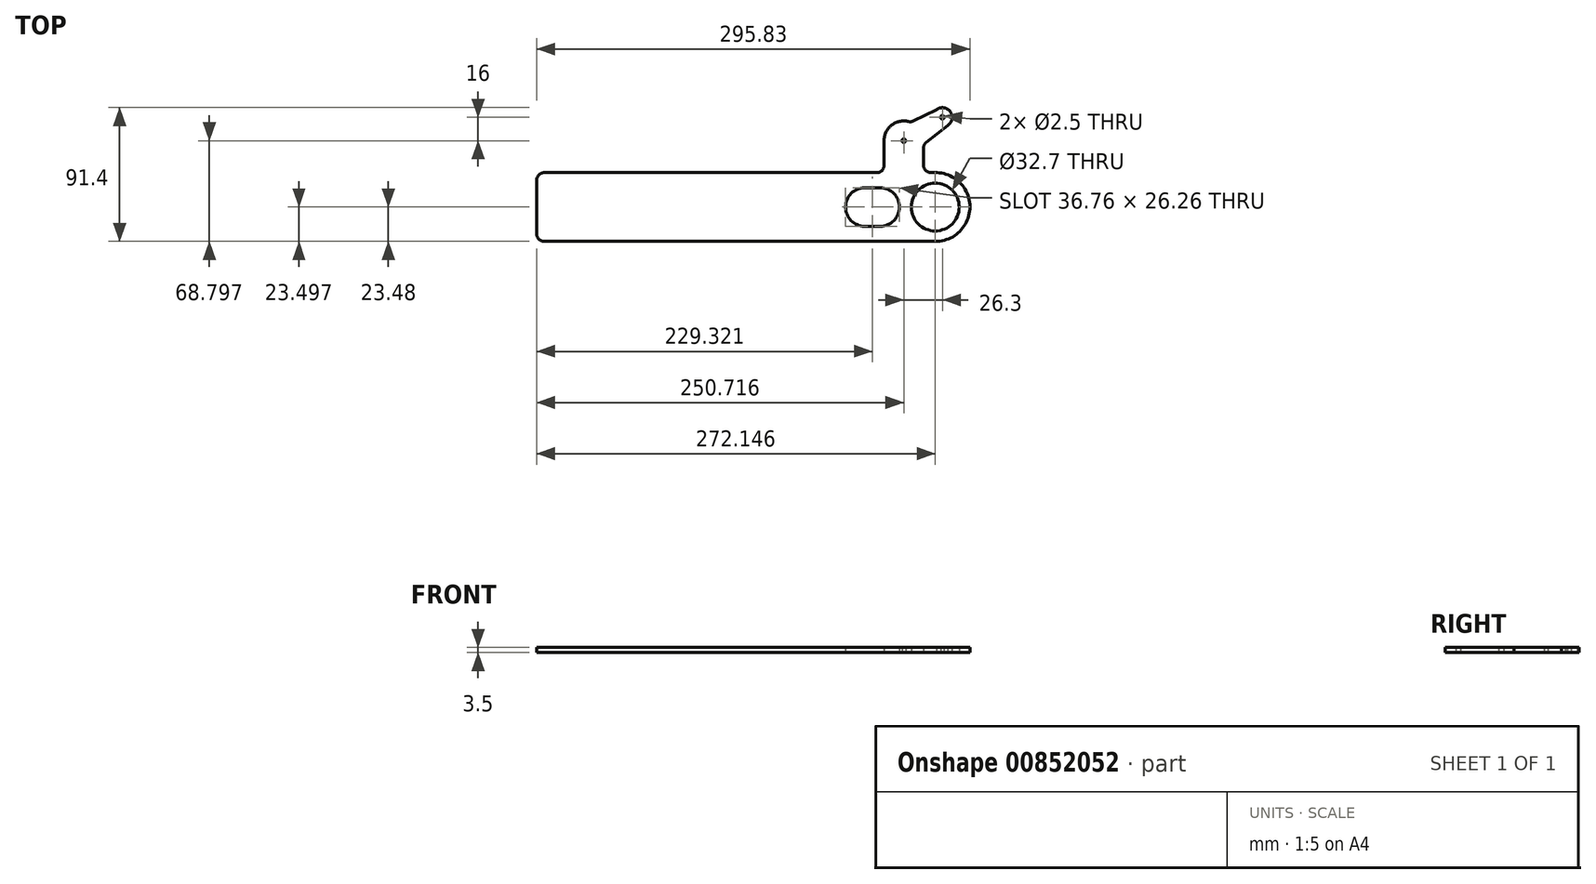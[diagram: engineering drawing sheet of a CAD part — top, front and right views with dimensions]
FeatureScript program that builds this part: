
annotation { "Feature Type Name" : "Feature", "Feature Type Description" : "" }
export const myFeature = defineFeature(function(context is Context, id is Id, definition is map)
    precondition{}
    {
        {
            var Q0;
            Q0=qCreatedBy(makeId("Top.planeOp"),FACE);
            var sketch = newSketch(context, id + "F0", { "sketchPlane" : qUnion([Q0])});
            skLineSegment(sketch, "E0", {"start": v(-113.09, -23.48) * mm, "end": v(154.06, -23.48) * mm});
            skLineSegment(sketch, "E1", {"start": v(-149.4, 0) * mm, "end": v(186.03, 0) * mm, "construction": true});
            skLineSegment(sketch, "E2", {"start": v(153.57, 23.5) * mm, "end": v(151.12, 23.5) * mm});
            skLineSegment(sketch, "E3", {"start": v(-118.09, 18.5) * mm, "end": v(-118.09, -18.48) * mm});
            skLineSegment(sketch, "E4", {"start": v(177.65, 0) * mm, "end": v(177.63, 118.47) * mm, "construction": true});
            skLineSegment(sketch, "E5", {"start": v(177.63, 118.47) * mm, "end": v(177.63, -94.2) * mm, "construction": true});
            skLineSegment(sketch, "E6", {"start": v(154.06, -23.48) * mm, "end": v(202.1, -23.48) * mm, "construction": true});
            skCircle(sketch, "E7", {"center": v(154.06, 0.02) * mm, "radius": 16.35 * mm});
            skCircle(sketch, "E8", {"center": v(132.63, 45.32) * mm, "radius": 1.25 * mm});
            skCircle(sketch, "E9", {"center": v(132.63, 45.32) * mm, "radius": 50.11 * mm, "construction": true});
            skArc(sketch, "E10", {"start": v(154.06, -23.48) * mm, "mid": v(177.74, 0.2) * mm, "end": v(153.69, 23.5) * mm});
            skLineSegment(sketch, "E11", {"start": v(119.13, 45.2) * mm, "end": v(119.13, 28.5) * mm});
            skLineSegment(sketch, "E12", {"start": v(146.12, 40.44) * mm, "end": v(146.12, 28.5) * mm});
            skLineSegment(sketch, "E13", {"start": v(132.63, 45.32) * mm, "end": v(158.93, 61.32) * mm, "construction": true});
            skCircle(sketch, "E14", {"center": v(158.93, 61.32) * mm, "radius": 1.25 * mm});
            skLineSegment(sketch, "E15", {"start": v(155.01, 66.63) * mm, "end": v(139.12, 58.82) * mm});
            skLineSegment(sketch, "E16", {"start": v(163.49, 56.55) * mm, "end": v(148.02, 44.36) * mm});
            skArc(sketch, "E17", {"start": v(162.5, 55.76) * mm, "mid": v(164.36, 65.06) * mm, "end": v(155.01, 66.63) * mm});
            skArc(sketch, "E18", {"start": v(135.76, 58.44) * mm, "mid": v(124.22, 55.87) * mm, "end": v(119.13, 45.2) * mm});
            skPoint(sketch, "E19.visualSharp", {"position": v(137.36, 57.95) * mm});
            skArc(sketch, "E19.filletArc", {"start": v(135.76, 58.44) * mm, "mid": v(137.47, 58.34) * mm, "end": v(139.12, 58.82) * mm});
            skArc(sketch, "E20.filletArc", {"start": v(148.02, 44.36) * mm, "mid": v(146.62, 42.62) * mm, "end": v(146.12, 40.44) * mm});
            skPoint(sketch, "E21.visualSharp", {"position": v(153.63, 23.5) * mm});
            skArc(sketch, "E21.filletArc", {"start": v(153.57, 23.5) * mm, "mid": v(153.63, 23.5) * mm, "end": v(153.69, 23.5) * mm});
            skArc(sketch, "E22.filletArc", {"start": v(146.12, 28.5) * mm, "mid": v(147.58, 24.97) * mm, "end": v(151.12, 23.5) * mm});
            skLineSegment(sketch, "E23", {"start": v(114.13, 23.5) * mm, "end": v(-113.09, 23.5) * mm});
            skPoint(sketch, "E24.visualSharp", {"position": v(119.13, 23.5) * mm});
            skArc(sketch, "E24.filletArc", {"start": v(114.13, 23.5) * mm, "mid": v(117.67, 24.97) * mm, "end": v(119.13, 28.5) * mm});
            skPoint(sketch, "E25.visualSharp", {"position": v(-118.09, 23.5) * mm});
            skArc(sketch, "E25.filletArc", {"start": v(-113.09, 23.5) * mm, "mid": v(-116.62, 22.04) * mm, "end": v(-118.09, 18.5) * mm});
            skPoint(sketch, "E26.visualSharp", {"position": v(-118.09, -23.48) * mm});
            skArc(sketch, "E26.filletArc", {"start": v(-118.09, -18.48) * mm, "mid": v(-116.62, -22.02) * mm, "end": v(-113.09, -23.48) * mm});
            skLineSegment(sketch, "E27", {"start": v(111.23, 13.13) * mm, "end": v(111.23, -16.56) * mm, "construction": true});
            skPoint(sketch, "E28.orphan", {"position": v(111.23, 0) * mm});
            skLineSegment(sketch, "E29", {"start": v(116.48, 11.38) * mm, "end": v(116.48, -18.09) * mm, "construction": true});
            skLineSegment(sketch, "E30", {"start": v(105.98, 13.13) * mm, "end": v(105.98, -18.09) * mm, "construction": true});
            skLineSegment(sketch, "E31", {"start": v(105.98, 13.13) * mm, "end": v(116.48, 13.13) * mm});
            skLineSegment(sketch, "E32", {"start": v(116.48, -13.13) * mm, "end": v(105.98, -13.13) * mm});
            skArc(sketch, "E33", {"start": v(105.98, 13.13) * mm, "mid": v(92.85, 0) * mm, "end": v(105.98, -13.13) * mm});
            skArc(sketch, "E34", {"start": v(116.48, -13.13) * mm, "mid": v(129.61, 0) * mm, "end": v(116.48, 13.13) * mm});
            skSolve(sketch);
        }
        {
            var Q0;
            Q0 = qSketchRegion(id + "F0", true);
            extrude(context, id + "F1", {"entities" : qUnion([Q0]), "depth" : 3.5 * mm, "offsetDistance" : 25 * mm});
        }
    });
